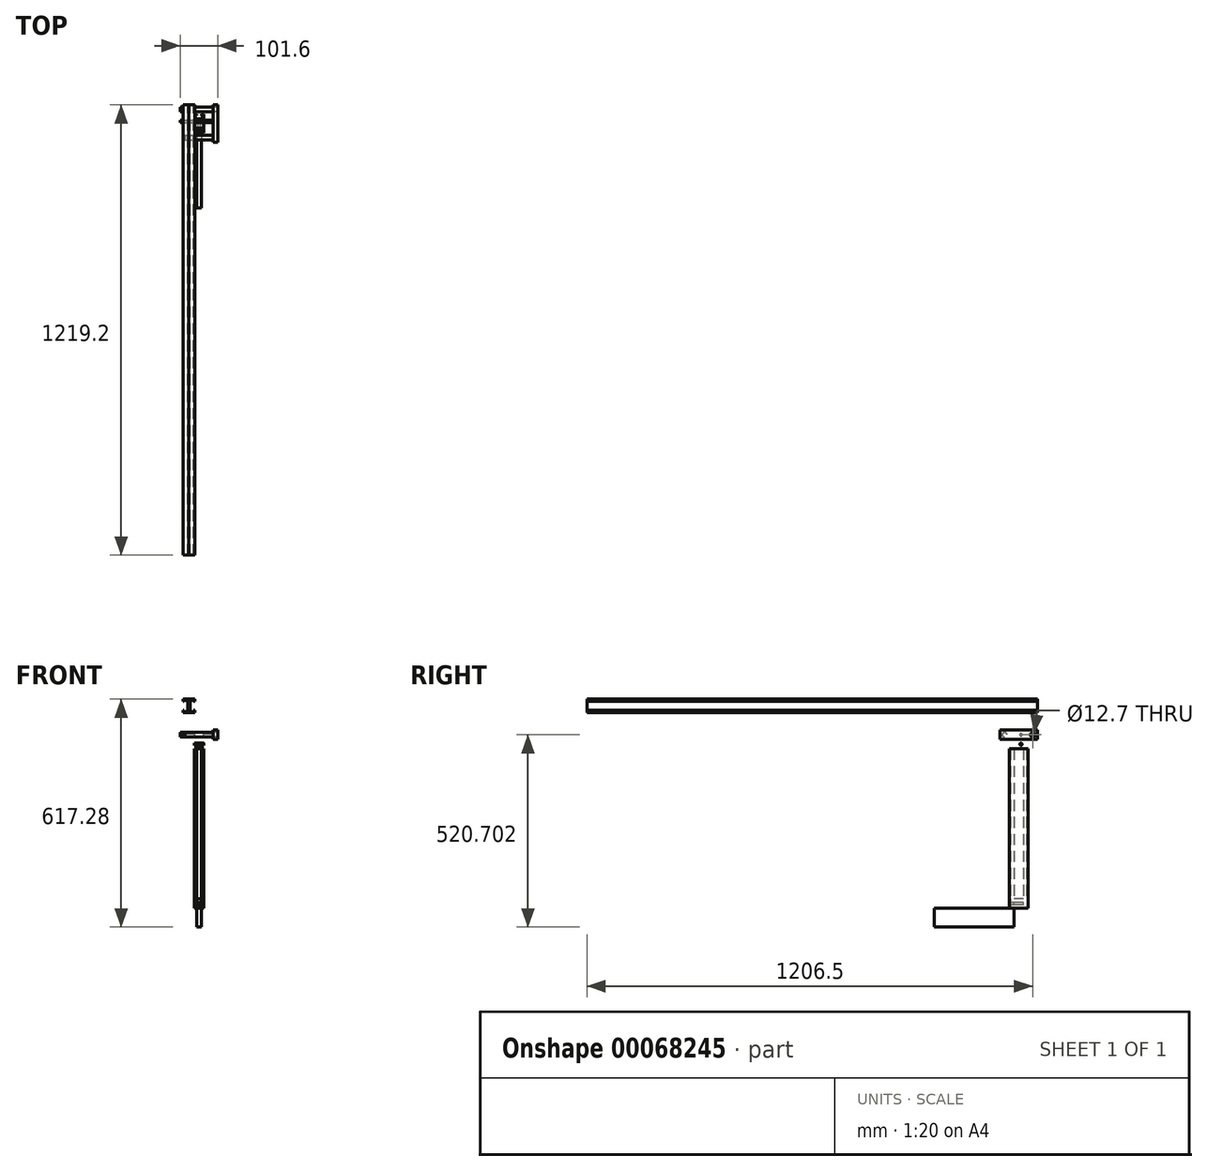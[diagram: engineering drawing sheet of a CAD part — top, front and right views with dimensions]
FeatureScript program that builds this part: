
annotation { "Feature Type Name" : "Feature", "Feature Type Description" : "" }
export const myFeature = defineFeature(function(context is Context, id is Id, definition is map)
    precondition{}
    {
        {
            var Q0;
            Q0=qCreatedBy(makeId("Front.planeOp"),FACE);
            var sketch = newSketch(context, id + "F0", { "sketchPlane" : qUnion([Q0])});
            skLineSegment(sketch, "E0", {"start": v(-25.85, 30.16) * mm, "end": v(-25.85, 36.51) * mm});
            skLineSegment(sketch, "E1", {"start": v(-25.85, 36.51) * mm, "end": v(-9.98, 36.51) * mm});
            skLineSegment(sketch, "E2", {"start": v(-9.98, 36.51) * mm, "end": v(-9.98, 0) * mm});
            skLineSegment(sketch, "E3", {"start": v(-9.98, 0) * mm, "end": v(-25.85, 0) * mm});
            skLineSegment(sketch, "E4", {"start": v(-25.85, 0) * mm, "end": v(-25.85, 6.35) * mm});
            skLineSegment(sketch, "E5", {"start": v(-25.85, 6.35) * mm, "end": v(-22.68, 6.35) * mm});
            skLineSegment(sketch, "E6", {"start": v(-22.68, 6.35) * mm, "end": v(-22.68, 3.17) * mm});
            skLineSegment(sketch, "E7", {"start": v(-22.68, 3.17) * mm, "end": v(-13.15, 3.18) * mm});
            skLineSegment(sketch, "E8", {"start": v(-25.85, 30.16) * mm, "end": v(-22.68, 30.16) * mm});
            skLineSegment(sketch, "E9", {"start": v(-22.68, 30.16) * mm, "end": v(-22.68, 33.34) * mm});
            skLineSegment(sketch, "E10", {"start": v(-13.15, 3.18) * mm, "end": v(-13.15, 33.34) * mm});
            skLineSegment(sketch, "E11", {"start": v(-13.15, 33.34) * mm, "end": v(-22.68, 33.34) * mm});
            skLineSegment(sketch, "E12", {"start": v(-9.98, 36.51) * mm, "end": v(-9.98, -22.06) * mm, "construction": true});
            skLineSegment(sketch, "E13.MirrorCS", {"start": v(-9.98, 0) * mm, "end": v(5.9, 0) * mm});
            skLineSegment(sketch, "E14.MirrorCS", {"start": v(5.9, 0) * mm, "end": v(5.9, 6.35) * mm});
            skLineSegment(sketch, "E15.MirrorCS", {"start": v(5.9, 6.35) * mm, "end": v(2.72, 6.35) * mm});
            skLineSegment(sketch, "E16.MirrorCS", {"start": v(2.72, 6.35) * mm, "end": v(2.72, 3.18) * mm});
            skLineSegment(sketch, "E17.MirrorCS", {"start": v(2.72, 3.18) * mm, "end": v(-6.8, 3.18) * mm});
            skLineSegment(sketch, "E18.MirrorCS", {"start": v(-6.8, 3.18) * mm, "end": v(-6.8, 33.34) * mm});
            skLineSegment(sketch, "E19.MirrorCS", {"start": v(-6.8, 33.34) * mm, "end": v(2.72, 33.34) * mm});
            skLineSegment(sketch, "E20.MirrorCS", {"start": v(2.72, 30.16) * mm, "end": v(2.72, 33.34) * mm});
            skLineSegment(sketch, "E21.MirrorCS", {"start": v(5.9, 30.16) * mm, "end": v(2.72, 30.16) * mm});
            skLineSegment(sketch, "E22.MirrorCS", {"start": v(5.9, 30.16) * mm, "end": v(5.9, 36.51) * mm});
            skLineSegment(sketch, "E23.MirrorCS", {"start": v(5.9, 36.51) * mm, "end": v(-9.98, 36.51) * mm});
            skSolve(sketch);
        }
        {
            var Q0;
            Q0=makeQuery(id+"F0.imprint","IMPRINT",FACE,{"disambiguationData":[TD([[makeQuery(id+"F0.imprint","IMPRINT",EDGE,{"derivedFrom":sQuery(id+"F0.wireOp",EDGE,"E0")}),-1.0]])]});
            extrude(context, id + "F1", {"entities" : qUnion([Q0]), "depth" : 1219.2 * mm});
        }
        {
            var Q0;
            Q0=makeQuery(id+"F0.imprint","IMPRINT",FACE,{"disambiguationData":[TD([[makeQuery(id+"F0.imprint","IMPRINT",EDGE,{"derivedFrom":sQuery(id+"F0.wireOp",EDGE,"E2")}),1.0]])]});
            extrude(context, id + "F2", {"entities" : qUnion([Q0]), "depth" : 1219.2 * mm});
        }
        {
            var Q0;
            Q0=qCreatedBy(makeId("Front.planeOp"),FACE);
            var sketch = newSketch(context, id + "F3", { "sketchPlane" : qUnion([Q0])});
            skLineSegment(sketch, "E24.bottom", {"start": v(-20.88, -47.37) * mm, "end": v(55.32, -47.37) * mm});
            skLineSegment(sketch, "E24.top", {"start": v(-20.88, -72.77) * mm, "end": v(55.32, -72.77) * mm});
            skLineSegment(sketch, "E24.left", {"start": v(-20.88, -47.37) * mm, "end": v(-20.88, -72.77) * mm});
            skLineSegment(sketch, "E24.right", {"start": v(55.32, -47.37) * mm, "end": v(55.32, -72.77) * mm});
            skSolve(sketch);
        }
        {
            var Q0;
            Q0=makeQuery(id+"F3.imprint","IMPRINT",FACE,{"disambiguationData":[TD([[makeQuery(id+"F3.imprint","IMPRINT",EDGE,{"derivedFrom":sQuery(id+"F3.wireOp",EDGE,"E24.bottom")}),-1.0]])]});
            extrude(context, id + "F4", {"entities" : qUnion([Q0]), "depth" : 101.6 * mm});
        }
        {
            var Q0;
            Q0=makeQuery(id+"F4.opExtrude","SWEPT_FACE",FACE,{"disambiguationData":[OSD([sQuery(id+"F3.wireOp",EDGE,"E24.right")])]});
            var sketch = newSketch(context, id + "F5", { "sketchPlane" : qUnion([Q0])});
            skLineSegment(sketch, "E25.0", {"start": v(-101.6, -47.37) * mm, "end": v(0, -47.37) * mm});
            skLineSegment(sketch, "E25.1", {"start": v(-101.6, -47.37) * mm, "end": v(-101.6, -72.77) * mm});
            skLineSegment(sketch, "E25.2", {"start": v(-101.6, -72.77) * mm, "end": v(0, -72.77) * mm});
            skLineSegment(sketch, "E25.3", {"start": v(0, -47.37) * mm, "end": v(0, -72.77) * mm});
            skLineSegment(sketch, "E26", {"start": v(-50.8, -47.37) * mm, "end": v(-50.8, -72.77) * mm, "construction": true});
            skCircle(sketch, "E27", {"center": v(-88.9, -60.07) * mm, "radius": 6.35 * mm});
            skLineSegment(sketch, "E28", {"start": v(-88.9, -47.37) * mm, "end": v(-88.9, -60.07) * mm, "construction": true});
            skLineSegment(sketch, "E29", {"start": v(-88.9, -60.07) * mm, "end": v(-101.6, -60.07) * mm, "construction": true});
            skCircle(sketch, "E30.MirrorC", {"center": v(-12.7, -60.07) * mm, "radius": 6.35 * mm});
            skSolve(sketch);
        }
        {
            var Q0;
            Q0=makeQuery(id+"F5.imprint","IMPRINT",FACE,{"disambiguationData":[TD([[makeQuery(id+"F5.imprint","IMPRINT",EDGE,{"derivedFrom":sQuery(id+"F5.wireOp",EDGE,"E27")}),1.0]])]});
            var Q1;
            Q1=makeQuery(id+"F5.imprint","IMPRINT",FACE,{"disambiguationData":[TD([[makeQuery(id+"F5.imprint","IMPRINT",EDGE,{"derivedFrom":sQuery(id+"F5.wireOp",EDGE,"E30.MirrorC")}),-1.0]])]});
            extrude(context, id + "F6", {"entities" : qUnion([Q0, Q1]), "operationType" : NewBodyOperationType.ADD, "depth" : 12.7 * mm});
        }
        {
            var Q0;
            Q0=makeQuery(id+"F4.opExtrude","SWEPT_FACE",FACE,{"disambiguationData":[OSD([sQuery(id+"F3.wireOp",EDGE,"E24.left")])]});
            var sketch = newSketch(context, id + "F7", { "sketchPlane" : qUnion([Q0])});
            skCircle(sketch, "E31.0", {"center": v(12.7, -60.07) * mm, "radius": 6.35 * mm});
            skCircle(sketch, "E31.1", {"center": v(88.9, -60.07) * mm, "radius": 6.35 * mm});
            skSolve(sketch);
        }
        {
            var Q0;
            Q0=makeQuery(id+"F7.imprint","IMPRINT",FACE,{"disambiguationData":[TD([[makeQuery(id+"F7.imprint","IMPRINT",EDGE,{"derivedFrom":sQuery(id+"F7.wireOp",EDGE,"E31.0")}),1.0]])]});
            var Q1;
            Q1=makeQuery(id+"F7.imprint","IMPRINT",FACE,{"disambiguationData":[TD([[makeQuery(id+"F7.imprint","IMPRINT",EDGE,{"derivedFrom":sQuery(id+"F7.wireOp",EDGE,"E31.1")}),-1.0]])]});
            extrude(context, id + "F8", {"entities" : qUnion([Q0, Q1]), "operationType" : NewBodyOperationType.ADD, "depth" : 12.7 * mm});
        }
        {
            var Q0;
            Q0=makeQuery(id+"F4.opExtrude","SWEPT_FACE",FACE,{"disambiguationData":[OSD([sQuery(id+"F3.wireOp",EDGE,"E24.top")])]});
            var sketch = newSketch(context, id + "F9", { "sketchPlane" : qUnion([Q0])});
            skLineSegment(sketch, "E32.0", {"start": v(55.32, 101.6) * mm, "end": v(55.32, 0) * mm});
            skLineSegment(sketch, "E32.1", {"start": v(-20.88, 0) * mm, "end": v(55.32, 0) * mm});
            skLineSegment(sketch, "E32.2", {"start": v(-20.88, 101.6) * mm, "end": v(-20.88, 0) * mm});
            skLineSegment(sketch, "E32.3", {"start": v(-20.88, 101.6) * mm, "end": v(55.32, 101.6) * mm});
            skLineSegment(sketch, "E33", {"start": v(17.22, 0) * mm, "end": v(17.22, 101.6) * mm, "construction": true});
            skLineSegment(sketch, "E34.rect.bottom", {"start": v(29.92, 25.4) * mm, "end": v(4.52, 25.4) * mm});
            skLineSegment(sketch, "E34.rect.top", {"start": v(29.92, 76.2) * mm, "end": v(4.52, 76.2) * mm});
            skLineSegment(sketch, "E34.rect.left", {"start": v(29.92, 25.4) * mm, "end": v(29.92, 76.2) * mm});
            skLineSegment(sketch, "E34.rect.right", {"start": v(4.52, 25.4) * mm, "end": v(4.52, 76.2) * mm});
            skPoint(sketch, "E34.rect.middle", {"position": v(17.22, 50.8) * mm});
            skSolve(sketch);
        }
        {
            var Q0;
            Q0=makeQuery(id+"F9.imprint","IMPRINT",FACE,{"disambiguationData":[TD([[makeQuery(id+"F9.imprint","IMPRINT",EDGE,{"derivedFrom":sQuery(id+"F9.wireOp",EDGE,"E34.rect.bottom")}),-1.0]])]});
            extrude(context, id + "F10", {"entities" : qUnion([Q0]), "operationType" : NewBodyOperationType.REMOVE, "oppositeDirection" : true, "depth" : 25.4 * mm});
        }
        {
            var Q0;
            Q0=makeQuery(id+"F5.imprint","IMPRINT",FACE,{"disambiguationData":[TD([[makeQuery(id+"F5.imprint","IMPRINT",EDGE,{"derivedFrom":sQuery(id+"F5.wireOp",EDGE,"E25.0")}),-1.0]])]});
            var sketch = newSketch(context, id + "F11", { "sketchPlane" : qUnion([Q0])});
            skLineSegment(sketch, "E35.0", {"start": v(-50.8, -47.37) * mm, "end": v(-50.8, -72.77) * mm, "construction": true});
            skLineSegment(sketch, "E35.1", {"start": v(-101.6, -47.37) * mm, "end": v(0, -47.37) * mm});
            skLineSegment(sketch, "E35.2", {"start": v(-101.6, -72.77) * mm, "end": v(0, -72.77) * mm});
            skCircle(sketch, "E36", {"center": v(-57.15, -60.07) * mm, "radius": 3.18 * mm});
            skCircle(sketch, "E37.MirrorC", {"center": v(-44.45, -60.07) * mm, "radius": 3.18 * mm});
            skSolve(sketch);
        }
        {
            var Q0;
            Q0=makeQuery(id+"F11.imprint","IMPRINT",FACE,{"disambiguationData":[TD([[makeQuery(id+"F11.imprint","IMPRINT",EDGE,{"derivedFrom":sQuery(id+"F11.wireOp",EDGE,"E36")}),1.0]])]});
            var Q1;
            Q1=makeQuery(id+"F11.imprint","IMPRINT",FACE,{"disambiguationData":[TD([[makeQuery(id+"F11.imprint","IMPRINT",EDGE,{"derivedFrom":sQuery(id+"F11.wireOp",EDGE,"E37.MirrorC")}),-1.0]])]});
            extrude(context, id + "F12", {"entities" : qUnion([Q0, Q1]), "operationType" : NewBodyOperationType.REMOVE, "endBound" : BoundingType.THROUGH_ALL, "oppositeDirection" : true, "depth" : 25.4 * mm});
        }
        {
            var Q0;
            Q0=makeQuery(id+"F4.opExtrude","SWEPT_FACE",FACE,{"disambiguationData":[OSD([sQuery(id+"F3.wireOp",EDGE,"E24.top")])]});
            var sketch = newSketch(context, id + "F13", { "sketchPlane" : qUnion([Q0])});
            skLineSegment(sketch, "E38.0", {"start": v(29.92, 25.4) * mm, "end": v(29.92, 76.2) * mm});
            skLineSegment(sketch, "E38.1", {"start": v(29.92, 76.2) * mm, "end": v(4.52, 76.2) * mm});
            skLineSegment(sketch, "E38.2", {"start": v(4.52, 25.4) * mm, "end": v(4.52, 76.2) * mm});
            skLineSegment(sketch, "E38.3", {"start": v(29.92, 25.4) * mm, "end": v(4.52, 25.4) * mm});
            skLineSegment(sketch, "E39.1", {"start": v(29.92, 25.4) * mm, "end": v(4.53, 25.4) * mm});
            skLineSegment(sketch, "E39.2", {"start": v(4.53, 25.4) * mm, "end": v(4.53, 76.2) * mm});
            skLineSegment(sketch, "E39.3", {"start": v(29.92, 76.2) * mm, "end": v(4.53, 76.2) * mm});
            skSolve(sketch);
        }
        {
            var Q0;
            Q0=makeQuery(id+"F13.imprint","IMPRINT",FACE,{"disambiguationData":[TD([[makeQuery(id+"F13.imprint","IMPRINT",EDGE,{"derivedFrom":sQuery(id+"F13.wireOp",EDGE,"E38.0")}),1.0]])]});
            extrude(context, id + "F14", {"entities" : qUnion([Q0]), "depth" : 457.2 * mm});
        }
        {
            var Q0;
            Q0=makeQuery(id+"F14.opExtrude","CAP_FACE",FACE,{"disambiguationData":[OSD([sQuery(id+"F13.wireOp",EDGE,"E38.0"),sQuery(id+"F13.wireOp",EDGE,"E39.1"),sQuery(id+"F13.wireOp",EDGE,"E39.2"),sQuery(id+"F13.wireOp",EDGE,"E39.3")])],"isStart":false});
            var sketch = newSketch(context, id + "F15", { "sketchPlane" : qUnion([Q0])});
            skLineSegment(sketch, "E40.0", {"start": v(29.92, 25.4) * mm, "end": v(29.92, 76.2) * mm});
            skLineSegment(sketch, "E40.2", {"start": v(4.53, 25.4) * mm, "end": v(4.53, 76.2) * mm});
            skLineSegment(sketch, "E40.3", {"start": v(29.92, 25.4) * mm, "end": v(4.53, 25.4) * mm});
            skLineSegment(sketch, "E40.4", {"start": v(29.92, 76.2) * mm, "end": v(4.53, 76.2) * mm});
            skLineSegment(sketch, "E41", {"start": v(23.57, 76.2) * mm, "end": v(23.57, 73.02) * mm});
            skLineSegment(sketch, "E42", {"start": v(23.57, 73.02) * mm, "end": v(26.74, 73.02) * mm});
            skLineSegment(sketch, "E43", {"start": v(26.74, 73.02) * mm, "end": v(26.74, 63.5) * mm});
            skLineSegment(sketch, "E44", {"start": v(26.74, 63.5) * mm, "end": v(7.7, 63.5) * mm});
            skLineSegment(sketch, "E45", {"start": v(7.7, 63.5) * mm, "end": v(7.7, 73.02) * mm});
            skLineSegment(sketch, "E46", {"start": v(7.7, 73.02) * mm, "end": v(10.88, 73.02) * mm});
            skLineSegment(sketch, "E47", {"start": v(10.88, 73.02) * mm, "end": v(10.88, 76.2) * mm});
            skLineSegment(sketch, "E48", {"start": v(29.92, 50.8) * mm, "end": v(4.53, 50.8) * mm, "construction": true});
            skLineSegment(sketch, "E49.MirrorCS", {"start": v(26.74, 38.1) * mm, "end": v(7.7, 38.1) * mm});
            skLineSegment(sketch, "E50.MirrorCS", {"start": v(26.74, 28.58) * mm, "end": v(26.74, 38.1) * mm});
            skLineSegment(sketch, "E51.MirrorCS", {"start": v(23.57, 28.58) * mm, "end": v(26.74, 28.58) * mm});
            skLineSegment(sketch, "E52.MirrorCS", {"start": v(23.57, 25.4) * mm, "end": v(23.57, 28.58) * mm});
            skLineSegment(sketch, "E53.MirrorCS", {"start": v(10.88, 28.58) * mm, "end": v(10.88, 25.4) * mm});
            skLineSegment(sketch, "E54.MirrorCS", {"start": v(7.7, 28.58) * mm, "end": v(10.88, 28.58) * mm});
            skLineSegment(sketch, "E55.MirrorCS", {"start": v(7.7, 38.1) * mm, "end": v(7.7, 28.58) * mm});
            skSolve(sketch);
        }
        {
            var Q0;
            {var subQ0=sQuery(id+"F15.wireOp",EDGE,"E41");Q0=makeQuery(id+"F15.imprint","IMPRINT",FACE,{"disambiguationData":[TD([[makeQuery(id+"F15.imprint","IMPRINT",EDGE,{"derivedFrom":subQ0}),-1.0]])]});}
            var Q1;
            Q1=makeQuery(id+"F15.imprint","IMPRINT",FACE,{"disambiguationData":[TD([[makeQuery(id+"F15.imprint","IMPRINT",EDGE,{"derivedFrom":sQuery(id+"F15.wireOp",EDGE,"E49.MirrorCS")}),1.0]])]});
            extrude(context, id + "F16", {"entities" : qUnion([Q0, Q1]), "operationType" : NewBodyOperationType.REMOVE, "endBound" : BoundingType.THROUGH_ALL, "oppositeDirection" : true, "depth" : 25.4 * mm});
        }
        {
            var Q0;
            Q0=makeQuery(id+"F14.opExtrude","SWEPT_FACE",FACE,{"disambiguationData":[OSD([sQuery(id+"F13.wireOp",EDGE,"E38.0")])]});
            var sketch = newSketch(context, id + "F17", { "sketchPlane" : qUnion([Q0])});
            skLineSegment(sketch, "E56.0", {"start": v(-76.2, -529.97) * mm, "end": v(-76.2, -72.77) * mm});
            skLineSegment(sketch, "E56.1", {"start": v(-25.4, -529.97) * mm, "end": v(-25.4, -72.77) * mm});
            skLineSegment(sketch, "E57", {"start": v(-76.2, -98.17) * mm, "end": v(-25.4, -98.17) * mm});
            skLineSegment(sketch, "E58.0", {"start": v(-25.4, -72.77) * mm, "end": v(-76.2, -72.77) * mm});
            skLineSegment(sketch, "E59", {"start": v(-50.8, -72.77) * mm, "end": v(-50.8, -98.17) * mm, "construction": true});
            skCircle(sketch, "E60", {"center": v(-57.15, -85.47) * mm, "radius": 3.18 * mm});
            skCircle(sketch, "E61.MirrorC", {"center": v(-44.45, -85.47) * mm, "radius": 3.18 * mm});
            skSolve(sketch);
        }
        {
            var Q0;
            Q0=makeQuery(id+"F17.imprint","IMPRINT",FACE,{"disambiguationData":[TD([[makeQuery(id+"F17.imprint","IMPRINT",EDGE,{"derivedFrom":sQuery(id+"F17.wireOp",EDGE,"E60")}),1.0]])]});
            var Q1;
            Q1=makeQuery(id+"F17.imprint","IMPRINT",FACE,{"disambiguationData":[TD([[makeQuery(id+"F17.imprint","IMPRINT",EDGE,{"derivedFrom":sQuery(id+"F17.wireOp",EDGE,"E61.MirrorC")}),-1.0]])]});
            extrude(context, id + "F18", {"entities" : qUnion([Q0, Q1]), "operationType" : NewBodyOperationType.REMOVE, "endBound" : BoundingType.THROUGH_ALL, "oppositeDirection" : true, "depth" : 25.4 * mm});
        }
        {
            var Q0;
            Q0=makeQuery(id+"F14.opExtrude","CAP_FACE",FACE,{"disambiguationData":[OSD([sQuery(id+"F13.wireOp",EDGE,"E38.0"),sQuery(id+"F13.wireOp",EDGE,"E39.1"),sQuery(id+"F13.wireOp",EDGE,"E39.2"),sQuery(id+"F13.wireOp",EDGE,"E39.3")])],"isStart":false});
            var sketch = newSketch(context, id + "F19", { "sketchPlane" : qUnion([Q0])});
            skLineSegment(sketch, "E62.0", {"start": v(29.92, 76.2) * mm, "end": v(4.52, 76.2) * mm});
            skLineSegment(sketch, "E63", {"start": v(26.74, 73.02) * mm, "end": v(26.74, 63.5) * mm});
            skLineSegment(sketch, "E64", {"start": v(26.74, 63.5) * mm, "end": v(7.7, 63.5) * mm});
            skLineSegment(sketch, "E65", {"start": v(7.7, 63.5) * mm, "end": v(7.7, 73.02) * mm});
            skLineSegment(sketch, "E66", {"start": v(7.7, 73.02) * mm, "end": v(10.88, 73.02) * mm});
            skLineSegment(sketch, "E67", {"start": v(10.88, 73.02) * mm, "end": v(10.88, 76.2) * mm});
            skLineSegment(sketch, "E68", {"start": v(26.74, 73.02) * mm, "end": v(23.56, 73.02) * mm});
            skLineSegment(sketch, "E69", {"start": v(23.56, 73.02) * mm, "end": v(23.56, 76.2) * mm});
            skSolve(sketch);
        }
        {
            var Q0;
            Q0=makeQuery(id+"F19.imprint","IMPRINT",FACE,{"disambiguationData":[TD([[makeQuery(id+"F19.imprint","IMPRINT",EDGE,{"derivedFrom":sQuery(id+"F19.wireOp",EDGE,"E63")}),-1.0]])]});
            var Q1;
            Q1=makeQuery(id+"F19.imprint","IMPRINT",FACE,{"disambiguationData":[TD([[makeQuery(id+"F19.imprint","IMPRINT",EDGE,{"derivedFrom":sQuery(id+"F19.wireOp",EDGE,"E63")}),-1.0]])]});
            extrude(context, id + "F20", {"entities" : qUnion([Q0, Q1]), "depth" : 50.8 * mm});
        }
        {
            var Q0;
            Q0=makeQuery(id+"F20.opExtrude","SWEPT_FACE",FACE,{"disambiguationData":[OSD([sQuery(id+"F19.wireOp",EDGE,"E62.0")])]});
            var sketch = newSketch(context, id + "F21", { "sketchPlane" : qUnion([Q0])});
            skLineSegment(sketch, "E70.0", {"start": v(23.56, -580.77) * mm, "end": v(23.56, -529.97) * mm});
            skLineSegment(sketch, "E70.1", {"start": v(23.56, -529.97) * mm, "end": v(10.88, -529.97) * mm});
            skLineSegment(sketch, "E70.2", {"start": v(10.88, -580.77) * mm, "end": v(10.88, -529.97) * mm});
            skLineSegment(sketch, "E70.3", {"start": v(23.56, -580.77) * mm, "end": v(10.88, -580.77) * mm});
            skSolve(sketch);
        }
        {
            var Q0;
            Q0=makeQuery(id+"F21.imprint","IMPRINT",FACE,{"disambiguationData":[TD([[makeQuery(id+"F21.imprint","IMPRINT",EDGE,{"derivedFrom":sQuery(id+"F21.wireOp",EDGE,"E70.0")}),1.0]])]});
            extrude(context, id + "F22", {"entities" : qUnion([Q0]), "operationType" : NewBodyOperationType.ADD, "depth" : 203.2 * mm});
        }
        {
            var Q0;
            Q0=makeQuery(id+"F22.boolean.opBoolean","MERGE",FACE,{"derivedFrom":[makeQuery(id+"F20.opExtrude","CAP_FACE",FACE,{"disambiguationData":[OSD([sQuery(id+"F19.wireOp",EDGE,"E62.0"),sQuery(id+"F19.wireOp",EDGE,"E63"),sQuery(id+"F19.wireOp",EDGE,"E64"),sQuery(id+"F19.wireOp",EDGE,"E65"),sQuery(id+"F19.wireOp",EDGE,"E66"),sQuery(id+"F19.wireOp",EDGE,"E67"),sQuery(id+"F19.wireOp",EDGE,"E68"),sQuery(id+"F19.wireOp",EDGE,"E69")])],"isStart":false}),makeQuery(id+"F22.opExtrude","SWEPT_FACE",FACE,{"disambiguationData":[OSD([sQuery(id+"F21.wireOp",EDGE,"E70.3")])]})]});
            var sketch = newSketch(context, id + "F23", { "sketchPlane" : qUnion([Q0])});
            skLineSegment(sketch, "E71.0", {"start": v(26.74, 73.02) * mm, "end": v(23.56, 73.02) * mm});
            skLineSegment(sketch, "E71.1", {"start": v(26.74, 73.02) * mm, "end": v(26.74, 63.5) * mm});
            skLineSegment(sketch, "E71.2", {"start": v(26.74, 63.5) * mm, "end": v(7.7, 63.5) * mm});
            skLineSegment(sketch, "E71.3", {"start": v(7.7, 63.5) * mm, "end": v(7.7, 73.02) * mm});
            skLineSegment(sketch, "E71.4", {"start": v(7.7, 73.02) * mm, "end": v(10.88, 73.02) * mm});
            skLineSegment(sketch, "E72", {"start": v(23.56, 73.02) * mm, "end": v(10.88, 73.02) * mm});
            skSolve(sketch);
        }
        {
            var Q0;
            Q0=makeQuery(id+"F23.imprint","IMPRINT",FACE,{"disambiguationData":[TD([[makeQuery(id+"F23.imprint","IMPRINT",EDGE,{"derivedFrom":sQuery(id+"F23.wireOp",EDGE,"E71.0")}),1.0]])]});
            extrude(context, id + "F24", {"entities" : qUnion([Q0]), "operationType" : NewBodyOperationType.ADD, "depth" : 25.4 * mm});
        }
        {
            var Q0;
            Q0=makeQuery(id+"F22.boolean.opBoolean","MERGE",FACE,{"derivedFrom":[makeQuery(id+"F20.opExtrude","CAP_FACE",FACE,{"disambiguationData":[OSD([sQuery(id+"F19.wireOp",EDGE,"E62.0"),sQuery(id+"F19.wireOp",EDGE,"E63"),sQuery(id+"F19.wireOp",EDGE,"E64"),sQuery(id+"F19.wireOp",EDGE,"E65"),sQuery(id+"F19.wireOp",EDGE,"E66"),sQuery(id+"F19.wireOp",EDGE,"E67"),sQuery(id+"F19.wireOp",EDGE,"E68"),sQuery(id+"F19.wireOp",EDGE,"E69")])],"isStart":true}),makeQuery(id+"F22.opExtrude","SWEPT_FACE",FACE,{"disambiguationData":[OSD([sQuery(id+"F21.wireOp",EDGE,"E70.1")])]})]});
            var sketch = newSketch(context, id + "F25", { "sketchPlane" : qUnion([Q0])});
            skLineSegment(sketch, "E73.0", {"start": v(26.74, -73.02) * mm, "end": v(7.7, -73.02) * mm});
            skLineSegment(sketch, "E73.1", {"start": v(26.74, -73.02) * mm, "end": v(26.74, -63.5) * mm});
            skLineSegment(sketch, "E74.0", {"start": v(26.74, -63.5) * mm, "end": v(7.7, -63.5) * mm});
            skLineSegment(sketch, "E74.1", {"start": v(7.7, -63.5) * mm, "end": v(7.7, -73.02) * mm});
            skSolve(sketch);
        }
        {
            var Q0;
            {var subQ0=sQuery(id+"F25.wireOp",EDGE,"E73.1");Q0=makeQuery(id+"F25.imprint","IMPRINT",FACE,{"disambiguationData":[TD([[makeQuery(id+"F25.imprint","IMPRINT",EDGE,{"derivedFrom":subQ0}),1.0]])]});}
            extrude(context, id + "F26", {"entities" : qUnion([Q0]), "operationType" : NewBodyOperationType.ADD, "depth" : 25.4 * mm});
        }
        {
            var Q0;
            Q0=makeQuery(id+"F26.boolean.opBoolean","MERGE",FACE,{"derivedFrom":[makeQuery(id+"F24.boolean.opBoolean","MERGE",FACE,{"derivedFrom":[makeQuery(id+"F20.opExtrude","SWEPT_FACE",FACE,{"disambiguationData":[OSD([sQuery(id+"F19.wireOp",EDGE,"E66")])]}),makeQuery(id+"F20.opExtrude","SWEPT_FACE",FACE,{"disambiguationData":[OSD([sQuery(id+"F19.wireOp",EDGE,"E68")])]}),makeQuery(id+"F24.opExtrude","SWEPT_FACE",FACE,{"disambiguationData":[OSD([sQuery(id+"F23.wireOp",EDGE,"E71.0"),sQuery(id+"F23.wireOp",EDGE,"E71.4"),sQuery(id+"F23.wireOp",EDGE,"E72")])]})]}),makeQuery(id+"F26.opExtrude","SWEPT_FACE",FACE,{"disambiguationData":[OSD([sQuery(id+"F25.wireOp",EDGE,"E73.0")])]})]});
            var sketch = newSketch(context, id + "F27", { "sketchPlane" : qUnion([Q0])});
            skLineSegment(sketch, "E75.0", {"start": v(26.74, -606.17) * mm, "end": v(26.74, -504.57) * mm});
            skLineSegment(sketch, "E75.1", {"start": v(7.7, -606.17) * mm, "end": v(7.7, -504.57) * mm});
            skLineSegment(sketch, "E75.2", {"start": v(26.74, -606.17) * mm, "end": v(7.7, -606.17) * mm});
            skLineSegment(sketch, "E75.3", {"start": v(26.74, -504.57) * mm, "end": v(7.7, -504.57) * mm});
            skLineSegment(sketch, "E76", {"start": v(26.74, -555.37) * mm, "end": v(7.7, -555.37) * mm, "construction": true});
            skCircle(sketch, "E77", {"center": v(17.21, -593.47) * mm, "radius": 3.18 * mm});
            skCircle(sketch, "E78.MirrorC", {"center": v(17.21, -517.27) * mm, "radius": 3.18 * mm});
            skSolve(sketch);
        }
        {
            var Q0;
            Q0=makeQuery(id+"F27.imprint","IMPRINT",FACE,{"disambiguationData":[TD([[makeQuery(id+"F27.imprint","IMPRINT",EDGE,{"derivedFrom":sQuery(id+"F27.wireOp",EDGE,"E78.MirrorC")}),-1.0]])]});
            var Q1;
            Q1=makeQuery(id+"F27.imprint","IMPRINT",FACE,{"disambiguationData":[TD([[makeQuery(id+"F27.imprint","IMPRINT",EDGE,{"derivedFrom":sQuery(id+"F27.wireOp",EDGE,"E77")}),1.0]])]});
            extrude(context, id + "F28", {"entities" : qUnion([Q0, Q1]), "operationType" : NewBodyOperationType.REMOVE, "endBound" : BoundingType.THROUGH_ALL, "oppositeDirection" : true, "depth" : 25.4 * mm});
        }
    });
